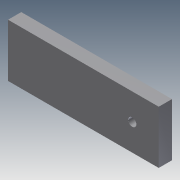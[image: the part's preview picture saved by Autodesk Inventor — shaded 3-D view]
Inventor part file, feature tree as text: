
AUTODESK INVENTOR PART (.ipt)
format: ipt  version: 2011 (Build 150239000, 239)  size: 98,816 bytes
history: native  units: in
note: dims shown in document units (in); Inventor stores cm internally (conversion verified against a paired STEP export)
features: extrude x5, sketch x5
ambient origin geometry x8: Origin, YZ Plane, XZ Plane, XY Plane, X Axis, Y Axis, Z Axis, Center Point
bodies: Solid1 (feature_tree)
feature tree (10):
  extrude  "Extrusion1"  Depth=1.0in
  extrude  "Extrusion2"  Depth=0.5in TaperAngle=0.0deg
  extrude  "Extrusion3"  Depth=0.156in
  extrude  "Extrusion4"  Depth=0.25in TaperAngle=0.0deg
  extrude  "Extrusion5"  [1 undecoded]
  sketch  "Sketch1"  dims[d0=2.0482in d1=1.0in]
  sketch  "Sketch2"  dims[d2=0.25in d3=0.0in d4=0.5in d5=0.0in]
  sketch  "Sketch3"  dims[d6=0.5in d7=0.156in]
  sketch  "Sketch4"  dims[d8=0.5in d9=0.0in d10=0.25in d11=0.0in]
  sketch  "Sketch5"  dims[d12=0.046in d13=0.0in]
note: 1 required parameter value undecoded (feature->parameter linkage not recoverable at this tier; creation-order binding heuristic only, values carry confidence <= 0.55)
